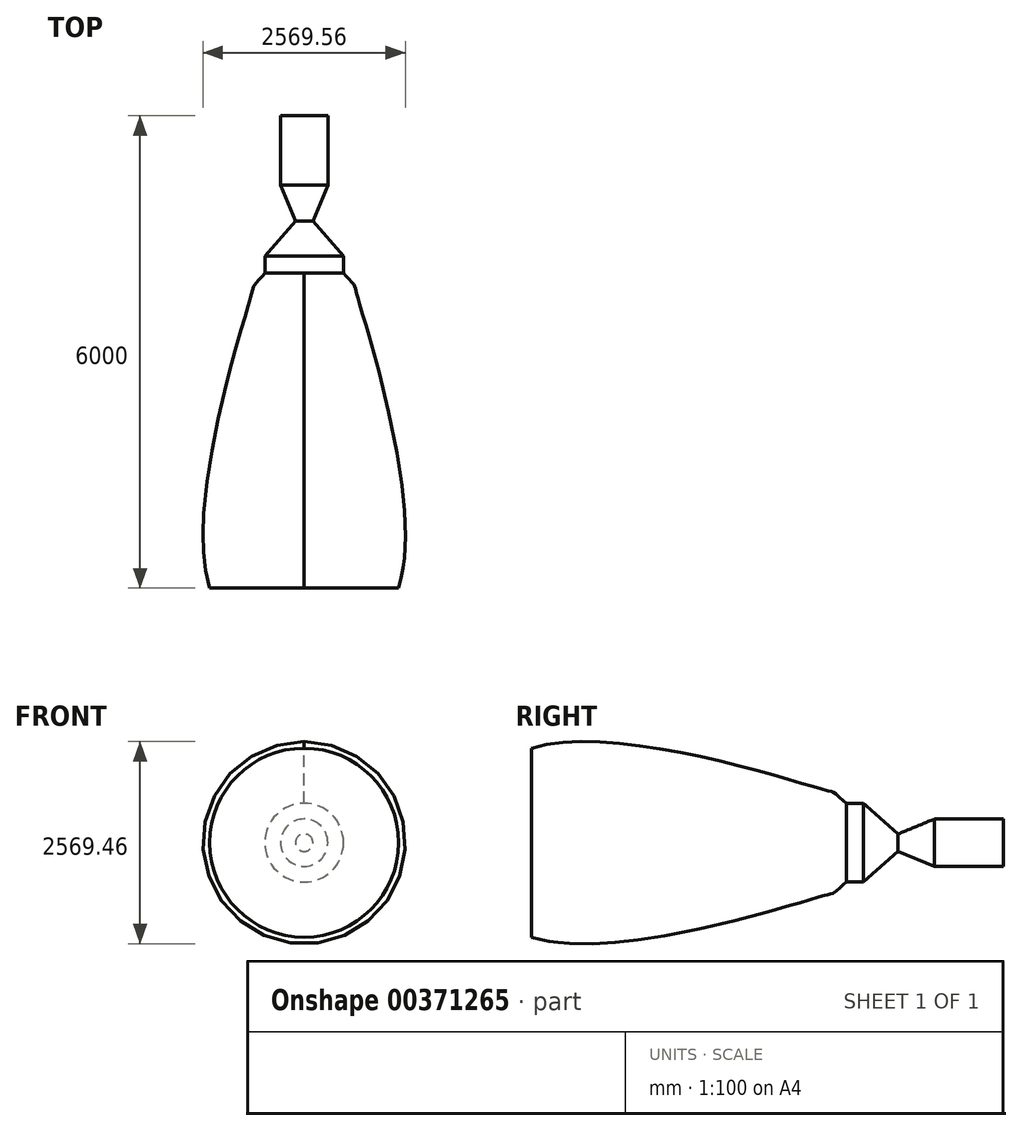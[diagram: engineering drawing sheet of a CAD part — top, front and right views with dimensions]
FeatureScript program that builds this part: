
annotation { "Feature Type Name" : "Feature", "Feature Type Description" : "" }
export const myFeature = defineFeature(function(context is Context, id is Id, definition is map)
    precondition{}
    {
        {
            var Q0;
            Q0=qCreatedBy(makeId("Right.planeOp"),FACE);
            var sketch = newSketch(context, id + "F0", { "sketchPlane" : qUnion([Q0])});
            skLineSegment(sketch, "E0", {"start": v(0, 0) * mm, "end": v(-4000, 0) * mm});
            skLineSegment(sketch, "E1", {"start": v(-4000, 1200) * mm, "end": v(-4000, 0) * mm});
            skLineSegment(sketch, "E2", {"start": v(0, 0) * mm, "end": v(0, 500) * mm});
            skFitSpline(sketch, "E3", {"points": [v(0, 500) * mm, v(-224.07, 656.67) * mm, v(-4000, 1200) * mm], "startDerivative": vector(-2576.08, 2303.81) * mm, "endDerivative": vector(-4161.92, -1302.73) * mm});
            skLineSegment(sketch, "E4.top", {"start": v(0, 0) * mm, "end": v(2000, 0) * mm});
            skLineSegment(sketch, "E4.left", {"start": v(0, 500) * mm, "end": v(0, 0) * mm});
            skLineSegment(sketch, "E4.right", {"start": v(2000, 300) * mm, "end": v(2000, 0) * mm});
            skLineSegment(sketch, "E5", {"start": v(2000, 300) * mm, "end": v(1120.27, 300) * mm});
            skLineSegment(sketch, "E6", {"start": v(1120.27, 300) * mm, "end": v(660.42, 111.26) * mm});
            skLineSegment(sketch, "E7", {"start": v(0, 500) * mm, "end": v(217, 500) * mm});
            skLineSegment(sketch, "E8", {"start": v(217, 500) * mm, "end": v(660.42, 111.26) * mm});
            skSolve(sketch);
        }
        {
            var Q0;
            Q0 = qSketchRegion(id + "F0", true);
            var Q1;
            Q1=sQuery(id+"F0.wireOp",EDGE,"E0");
            revolve(context, id + "F1", {"entities" : qUnion([Q0]), "axis" : qUnion([Q1]), "revolveType" : RevolveType.FULL});
        }
    });
